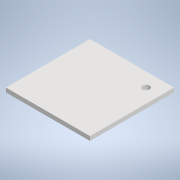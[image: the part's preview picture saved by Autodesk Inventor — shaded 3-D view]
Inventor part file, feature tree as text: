
AUTODESK INVENTOR PART (.ipt)
format: ipt  version: 2020 (Build 240168000, 168)  size: 114,688 bytes
history: native  units: in
note: dims shown in document units (in); Inventor stores cm internally (conversion verified against a paired STEP export)
features: extrude x3, sketch x3, fillet x1
ambient origin geometry x8: Origin, YZ Plane, XZ Plane, XY Plane, X Axis, Y Axis, Z Axis, Center Point
bodies: Solid1 (feature_tree)
feature tree (7):
  extrude  "Extrusion1"  Depth=3.0in
  extrude  "Extrusion2"  Depth=1.0in
  extrude  "Extrusion3"  Depth=0.15in TaperAngle=0.0deg
  fillet  "Fillet1"  Radius=1.0in
  sketch  "Sketch1"  dims[d0=3.0in d1=3.0in]
  sketch  "Sketch2"  dims[d2=0.15in d3=0.0in d4=1.0in]
  sketch  "Sketch3"  dims[d5=0.15in d6=0.0in d7=0.15in d8=0.0in d9=1.0in]
